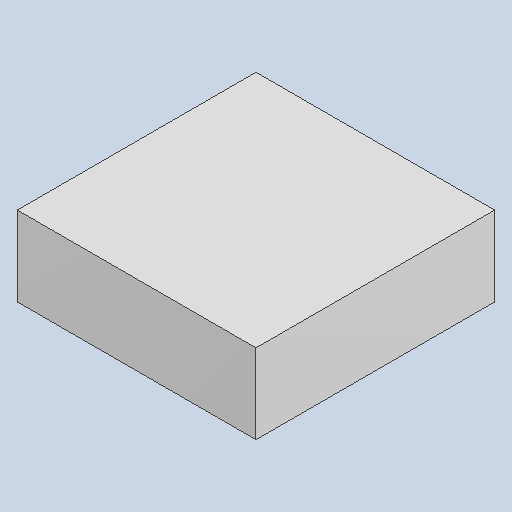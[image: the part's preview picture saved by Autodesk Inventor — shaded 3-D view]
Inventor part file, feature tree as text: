
AUTODESK INVENTOR PART (.ipt)
format: ipt  version: 2023.4 (Build 274418000, 418)  size: 79,872 bytes
history: native  units: mm
features: extrude x1
ambient origin geometry x8: Origin, YZ Plane, XZ Plane, XY Plane, X Axis, Y Axis, Z Axis, Center Point
bodies: Solid1 (feature_tree)
feature tree (1):
  extrude  "Extruded_33"  [1 undecoded]
note: 1 required parameter value undecoded (feature->parameter linkage not recoverable at this tier; creation-order binding heuristic only, values carry confidence <= 0.55)
